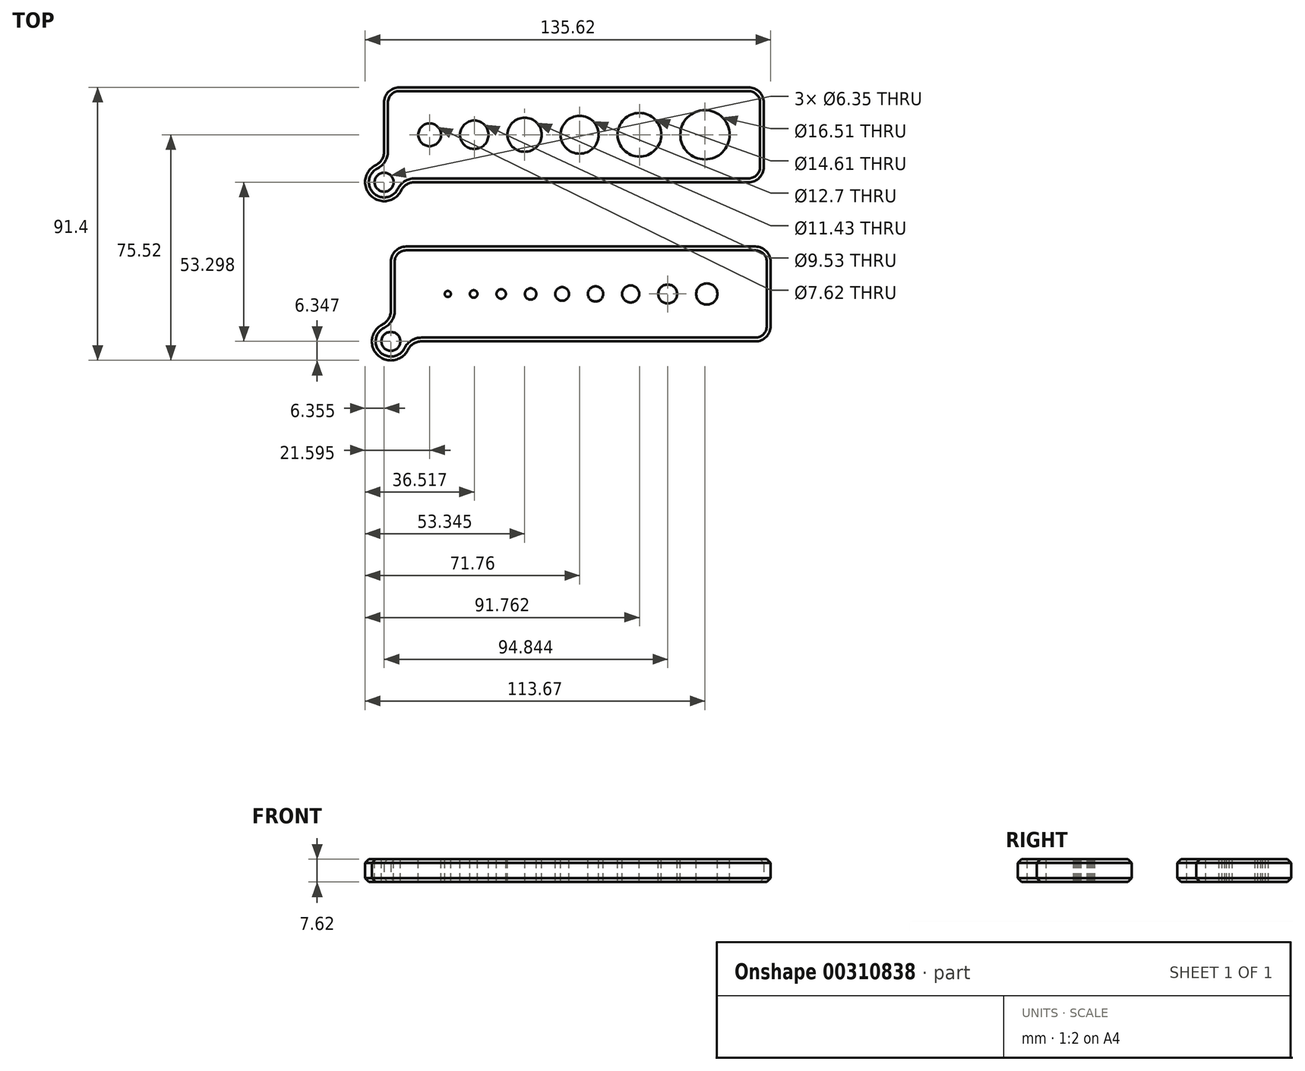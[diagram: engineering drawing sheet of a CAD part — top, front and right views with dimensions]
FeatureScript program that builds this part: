
annotation { "Feature Type Name" : "Feature", "Feature Type Description" : "" }
export const myFeature = defineFeature(function(context is Context, id is Id, definition is map)
    precondition{}
    {
        {
            var Q0;
            Q0=qCreatedBy(makeId("Top.planeOp"),FACE);
            var sketch = newSketch(context, id + "F0", { "sketchPlane" : qUnion([Q0])});
            skLineSegment(sketch, "E0.bottom", {"start": v(-62.35, 8.82) * mm, "end": v(64.65, 8.82) * mm});
            skLineSegment(sketch, "E0.top", {"start": v(-62.35, -22.93) * mm, "end": v(64.65, -22.93) * mm});
            skLineSegment(sketch, "E0.left", {"start": v(-62.35, 8.82) * mm, "end": v(-62.35, -22.93) * mm});
            skLineSegment(sketch, "E0.right", {"start": v(64.65, 8.82) * mm, "end": v(64.65, -22.93) * mm});
            skSolve(sketch);
        }
        {
            var Q0;
            Q0=makeQuery(id+"F0.imprint","IMPRINT",FACE,{"disambiguationData":[TD([[makeQuery(id+"F0.imprint","IMPRINT",EDGE,{"derivedFrom":sQuery(id+"F0.wireOp",EDGE,"E0.bottom")}),-1.0]])]});
            extrude(context, id + "F1", {"entities" : qUnion([Q0]), "depth" : 7.62 * mm});
        }
        {
            var Q0;
            Q0=makeQuery(id+"F1.opExtrude","CAP_FACE",FACE,{"disambiguationData":[OSD([sQuery(id+"F0.wireOp",EDGE,"E0.bottom"),sQuery(id+"F0.wireOp",EDGE,"E0.top"),sQuery(id+"F0.wireOp",EDGE,"E0.left"),sQuery(id+"F0.wireOp",EDGE,"E0.right")])],"isStart":false});
            var sketch = newSketch(context, id + "F2", { "sketchPlane" : qUnion([Q0])});
            skCircle(sketch, "E1", {"center": v(-43.3, -7.06) * mm, "radius": 1.02 * mm});
            skCircle(sketch, "E2", {"center": v(-34.67, -7.06) * mm, "radius": 1.27 * mm});
            skCircle(sketch, "E3", {"center": v(-25.46, -7.06) * mm, "radius": 1.59 * mm});
            skCircle(sketch, "E4", {"center": v(-15.62, -7.06) * mm, "radius": 1.9 * mm});
            skCircle(sketch, "E5", {"center": v(-5.08, -7.06) * mm, "radius": 2.29 * mm});
            skCircle(sketch, "E6", {"center": v(6.1, -7.06) * mm, "radius": 2.54 * mm});
            skCircle(sketch, "E7", {"center": v(17.85, -7.06) * mm, "radius": 2.86 * mm});
            skCircle(sketch, "E8", {"center": v(30.23, -7.06) * mm, "radius": 3.18 * mm});
            skCircle(sketch, "E9", {"center": v(43.31, -7.06) * mm, "radius": 3.56 * mm});
            skSolve(sketch);
        }
        {
            var Q0;
            Q0 = qSketchRegion(id + "F2", true);
            extrude(context, id + "F3", {"entities" : qUnion([Q0]), "operationType" : NewBodyOperationType.REMOVE, "oppositeDirection" : true, "depth" : 25.4 * mm});
        }
        {
            var Q0;
            Q0=qCreatedBy(makeId("Top.planeOp"),FACE);
            var sketch = newSketch(context, id + "F4", { "sketchPlane" : qUnion([Q0])});
            skLineSegment(sketch, "E10.bottom", {"start": v(-64.62, 62.12) * mm, "end": v(62.38, 62.12) * mm});
            skLineSegment(sketch, "E10.top", {"start": v(-64.62, 30.37) * mm, "end": v(62.38, 30.37) * mm});
            skLineSegment(sketch, "E10.left", {"start": v(-64.62, 62.12) * mm, "end": v(-64.62, 30.37) * mm});
            skLineSegment(sketch, "E10.right", {"start": v(62.38, 62.12) * mm, "end": v(62.38, 30.37) * mm});
            skSolve(sketch);
        }
        {
            var Q0;
            Q0=makeQuery(id+"F4.imprint","IMPRINT",FACE,{"disambiguationData":[TD([[makeQuery(id+"F4.imprint","IMPRINT",EDGE,{"derivedFrom":sQuery(id+"F4.wireOp",EDGE,"E10.bottom")}),-1.0]])]});
            extrude(context, id + "F5", {"entities" : qUnion([Q0]), "depth" : 7.62 * mm});
        }
        {
            var Q0;
            Q0=makeQuery(id+"F5.opExtrude","CAP_FACE",FACE,{"disambiguationData":[OSD([sQuery(id+"F4.wireOp",EDGE,"E10.bottom"),sQuery(id+"F4.wireOp",EDGE,"E10.top"),sQuery(id+"F4.wireOp",EDGE,"E10.left"),sQuery(id+"F4.wireOp",EDGE,"E10.right")])],"isStart":false});
            var sketch = newSketch(context, id + "F6", { "sketchPlane" : qUnion([Q0])});
            skCircle(sketch, "E11", {"center": v(-49.38, 46.24) * mm, "radius": 3.81 * mm});
            skPoint(sketch, "E11.centerSnap0", {"position": v(-64.62, 46.24) * mm});
            skCircle(sketch, "E12", {"center": v(-34.45, 46.24) * mm, "radius": 4.76 * mm});
            skCircle(sketch, "E13", {"center": v(-17.63, 46.24) * mm, "radius": 5.72 * mm});
            skCircle(sketch, "E14", {"center": v(0.79, 46.24) * mm, "radius": 6.35 * mm});
            skCircle(sketch, "E15", {"center": v(20.8, 46.24) * mm, "radius": 7.3 * mm});
            skCircle(sketch, "E16", {"center": v(42.7, 46.24) * mm, "radius": 8.26 * mm});
            skSolve(sketch);
        }
        {
            var Q0;
            Q0 = qSketchRegion(id + "F6", true);
            extrude(context, id + "F7", {"entities" : qUnion([Q0]), "operationType" : NewBodyOperationType.REMOVE, "oppositeDirection" : true, "depth" : 25.4 * mm});
        }
        {
            var Q0;
            Q0=makeQuery(id+"F5.opExtrude","CAP_FACE",FACE,{"disambiguationData":[OSD([sQuery(id+"F4.wireOp",EDGE,"E10.bottom"),sQuery(id+"F4.wireOp",EDGE,"E10.top"),sQuery(id+"F4.wireOp",EDGE,"E10.left"),sQuery(id+"F4.wireOp",EDGE,"E10.right")])],"isStart":false});
            var sketch = newSketch(context, id + "F8", { "sketchPlane" : qUnion([Q0])});
            skLineSegment(sketch, "E17.bottom", {"start": v(-64.62, 30.37) * mm, "end": v(-70.97, 30.37) * mm});
            skLineSegment(sketch, "E17.top", {"start": v(-64.62, 24.02) * mm, "end": v(-70.97, 24.02) * mm});
            skLineSegment(sketch, "E17.left", {"start": v(-64.62, 30.37) * mm, "end": v(-64.62, 24.02) * mm});
            skLineSegment(sketch, "E17.right", {"start": v(-70.97, 30.37) * mm, "end": v(-70.97, 24.02) * mm});
            skLineSegment(sketch, "E18.bottom", {"start": v(-70.97, 30.37) * mm, "end": v(-64.62, 30.37) * mm});
            skLineSegment(sketch, "E18.top", {"start": v(-70.97, 36.72) * mm, "end": v(-64.62, 36.72) * mm});
            skLineSegment(sketch, "E18.left", {"start": v(-70.97, 30.37) * mm, "end": v(-70.97, 36.72) * mm});
            skLineSegment(sketch, "E18.right", {"start": v(-64.62, 30.37) * mm, "end": v(-64.62, 36.72) * mm});
            skLineSegment(sketch, "E19.bottom", {"start": v(-64.62, 24.02) * mm, "end": v(-58.27, 24.02) * mm});
            skLineSegment(sketch, "E19.top", {"start": v(-64.62, 30.37) * mm, "end": v(-58.27, 30.37) * mm});
            skLineSegment(sketch, "E19.left", {"start": v(-64.62, 24.02) * mm, "end": v(-64.62, 30.37) * mm});
            skLineSegment(sketch, "E19.right", {"start": v(-58.27, 24.02) * mm, "end": v(-58.27, 30.37) * mm});
            skSolve(sketch);
        }
        {
            var Q0;
            Q0 = qSketchRegion(id + "F8", true);
            extrude(context, id + "F9", {"entities" : qUnion([Q0]), "oppositeDirection" : true, "depth" : 7.62 * mm});
        }
        {
            var Q0;
            Q0=makeQuery(id+"F9.opExtrude","SWEPT_BODY",BODY,{"disambiguationData":[OSD([sQuery(id+"F8.wireOp",EDGE,"E17.top"),sQuery(id+"F8.wireOp",EDGE,"E17.right"),sQuery(id+"F8.wireOp",EDGE,"E18.top"),sQuery(id+"F8.wireOp",EDGE,"E18.left"),sQuery(id+"F8.wireOp",EDGE,"E18.right"),sQuery(id+"F8.wireOp",EDGE,"E19.bottom"),sQuery(id+"F8.wireOp",EDGE,"E19.top"),sQuery(id+"F8.wireOp",EDGE,"E19.right")])]});
            var Q1;
            Q1=makeQuery(id+"F5.opExtrude","SWEPT_BODY",BODY,{"disambiguationData":[OSD([sQuery(id+"F4.wireOp",EDGE,"E10.bottom"),sQuery(id+"F4.wireOp",EDGE,"E10.top"),sQuery(id+"F4.wireOp",EDGE,"E10.left"),sQuery(id+"F4.wireOp",EDGE,"E10.right")])]});
            booleanBodies(context, id + "F10", {"operationType" : BooleanOperationType.UNION, "tools" : qUnion([Q0, Q1])});
        }
        {
            var Q0;
            Q0=makeQuery(id+"F9.opExtrude","SWEPT_EDGE",EDGE,{"disambiguationData":[OSD([sQuery(id+"F8.wireOp",EDGE,"E19.bottom"),sQuery(id+"F8.wireOp",EDGE,"E19.right")])]});
            var Q1;
            Q1=makeQuery(id+"F9.opExtrude","SWEPT_EDGE",EDGE,{"disambiguationData":[OSD([sQuery(id+"F8.wireOp",EDGE,"E17.top"),sQuery(id+"F8.wireOp",EDGE,"E17.right")])]});
            var Q2;
            Q2=makeQuery(id+"F9.opExtrude","SWEPT_EDGE",EDGE,{"disambiguationData":[OSD([sQuery(id+"F8.wireOp",EDGE,"E18.top"),sQuery(id+"F8.wireOp",EDGE,"E18.left")])]});
            fillet(context, id + "F11", {"entities" : qUnion([Q0, Q1, Q2]), "radius" : 6.35 * mm, "tangentPropagation" : true, "allowEdgeOverflow" : false});
        }
        {
            var Q0;
            Q0=makeQuery(id+"F1.opExtrude","CAP_FACE",FACE,{"disambiguationData":[OSD([sQuery(id+"F0.wireOp",EDGE,"E0.bottom"),sQuery(id+"F0.wireOp",EDGE,"E0.top"),sQuery(id+"F0.wireOp",EDGE,"E0.left"),sQuery(id+"F0.wireOp",EDGE,"E0.right")])],"isStart":false});
            var sketch = newSketch(context, id + "F12", { "sketchPlane" : qUnion([Q0])});
            skLineSegment(sketch, "E20.bottom", {"start": v(-62.35, -22.93) * mm, "end": v(-68.7, -22.93) * mm});
            skLineSegment(sketch, "E20.top", {"start": v(-62.35, -29.28) * mm, "end": v(-68.7, -29.28) * mm});
            skLineSegment(sketch, "E20.left", {"start": v(-62.35, -22.93) * mm, "end": v(-62.35, -29.28) * mm});
            skLineSegment(sketch, "E20.right", {"start": v(-68.7, -22.93) * mm, "end": v(-68.7, -29.28) * mm});
            skLineSegment(sketch, "E21.bottom", {"start": v(-62.35, -29.28) * mm, "end": v(-56, -29.28) * mm});
            skLineSegment(sketch, "E21.top", {"start": v(-62.35, -22.93) * mm, "end": v(-56, -22.93) * mm});
            skLineSegment(sketch, "E21.left", {"start": v(-62.35, -29.28) * mm, "end": v(-62.35, -22.93) * mm});
            skLineSegment(sketch, "E21.right", {"start": v(-56, -29.28) * mm, "end": v(-56, -22.93) * mm});
            skLineSegment(sketch, "E22.bottom", {"start": v(-68.7, -22.93) * mm, "end": v(-62.35, -22.93) * mm});
            skLineSegment(sketch, "E22.top", {"start": v(-68.7, -16.58) * mm, "end": v(-62.35, -16.58) * mm});
            skLineSegment(sketch, "E22.left", {"start": v(-68.7, -22.93) * mm, "end": v(-68.7, -16.58) * mm});
            skLineSegment(sketch, "E22.right", {"start": v(-62.35, -22.93) * mm, "end": v(-62.35, -16.58) * mm});
            skSolve(sketch);
        }
        {
            var Q0;
            Q0 = qSketchRegion(id + "F12", true);
            extrude(context, id + "F13", {"entities" : qUnion([Q0]), "operationType" : NewBodyOperationType.ADD, "oppositeDirection" : true, "depth" : 7.62 * mm});
        }
        {
            var Q0;
            Q0=makeQuery(id+"F13.opExtrude","SWEPT_EDGE",EDGE,{"disambiguationData":[OSD([sQuery(id+"F12.wireOp",EDGE,"E21.bottom"),sQuery(id+"F12.wireOp",EDGE,"E21.right")])]});
            var Q1;
            Q1=makeQuery(id+"F13.opExtrude","SWEPT_EDGE",EDGE,{"disambiguationData":[OSD([sQuery(id+"F12.wireOp",EDGE,"E20.top"),sQuery(id+"F12.wireOp",EDGE,"E20.right")])]});
            var Q2;
            Q2=makeQuery(id+"F13.opExtrude","SWEPT_EDGE",EDGE,{"disambiguationData":[OSD([sQuery(id+"F12.wireOp",EDGE,"E22.top"),sQuery(id+"F12.wireOp",EDGE,"E22.left")])]});
            fillet(context, id + "F14", {"entities" : qUnion([Q0, Q1, Q2]), "radius" : 6.35 * mm, "tangentPropagation" : true, "allowEdgeOverflow" : false});
        }
        {
            var Q0;
            Q0=makeQuery(id+"F13.boolean.opBoolean","MERGE",FACE,{"derivedFrom":[makeQuery(id+"F1.opExtrude","CAP_FACE",FACE,{"disambiguationData":[OSD([sQuery(id+"F0.wireOp",EDGE,"E0.bottom"),sQuery(id+"F0.wireOp",EDGE,"E0.top"),sQuery(id+"F0.wireOp",EDGE,"E0.left"),sQuery(id+"F0.wireOp",EDGE,"E0.right")])],"isStart":false}),makeQuery(id+"F13.opExtrude","CAP_FACE",FACE,{"disambiguationData":[OSD([sQuery(id+"F12.wireOp",EDGE,"E20.top"),sQuery(id+"F12.wireOp",EDGE,"E20.right"),sQuery(id+"F12.wireOp",EDGE,"E21.bottom"),sQuery(id+"F12.wireOp",EDGE,"E21.top"),sQuery(id+"F12.wireOp",EDGE,"E21.right"),sQuery(id+"F12.wireOp",EDGE,"E22.top"),sQuery(id+"F12.wireOp",EDGE,"E22.left"),sQuery(id+"F12.wireOp",EDGE,"E22.right")])],"isStart":true})]});
            var sketch = newSketch(context, id + "F15", { "sketchPlane" : qUnion([Q0])});
            skCircle(sketch, "E23", {"center": v(-62.35, -22.93) * mm, "radius": 3.18 * mm});
            skSolve(sketch);
        }
        {
            var Q0;
            Q0=makeQuery(id+"F10.opBoolean","MERGE",FACE,{"derivedFrom":[makeQuery(id+"F5.opExtrude","CAP_FACE",FACE,{"disambiguationData":[OSD([sQuery(id+"F4.wireOp",EDGE,"E10.bottom"),sQuery(id+"F4.wireOp",EDGE,"E10.top"),sQuery(id+"F4.wireOp",EDGE,"E10.left"),sQuery(id+"F4.wireOp",EDGE,"E10.right")])],"isStart":false}),makeQuery(id+"F9.opExtrude","CAP_FACE",FACE,{"disambiguationData":[OSD([sQuery(id+"F8.wireOp",EDGE,"E17.top"),sQuery(id+"F8.wireOp",EDGE,"E17.right"),sQuery(id+"F8.wireOp",EDGE,"E18.top"),sQuery(id+"F8.wireOp",EDGE,"E18.left"),sQuery(id+"F8.wireOp",EDGE,"E18.right"),sQuery(id+"F8.wireOp",EDGE,"E19.bottom"),sQuery(id+"F8.wireOp",EDGE,"E19.top"),sQuery(id+"F8.wireOp",EDGE,"E19.right")])],"isStart":true})]});
            var sketch = newSketch(context, id + "F16", { "sketchPlane" : qUnion([Q0])});
            skCircle(sketch, "E24", {"center": v(-64.62, 30.37) * mm, "radius": 3.18 * mm});
            skSolve(sketch);
        }
        {
            var Q0;
            Q0=makeQuery(id+"F16.imprint","IMPRINT",FACE,{"disambiguationData":[TD([[makeQuery(id+"F16.imprint","IMPRINT",EDGE,{"derivedFrom":sQuery(id+"F16.wireOp",EDGE,"E24")}),1.0]])]});
            extrude(context, id + "F17", {"entities" : qUnion([Q0]), "operationType" : NewBodyOperationType.REMOVE, "oppositeDirection" : true, "depth" : 25.4 * mm});
        }
        {
            var Q0;
            Q0=makeQuery(id+"F15.imprint","IMPRINT",FACE,{"disambiguationData":[TD([[makeQuery(id+"F15.imprint","IMPRINT",EDGE,{"derivedFrom":sQuery(id+"F15.wireOp",EDGE,"E23")}),1.0]])]});
            extrude(context, id + "F18", {"entities" : qUnion([Q0]), "operationType" : NewBodyOperationType.REMOVE, "oppositeDirection" : true, "depth" : 25.4 * mm});
        }
        {
            var Q0;
            Q0=makeQuery(id+"F14.opFillet","BLEND_EDGE",EDGE,{"blendedFrom":[makeQuery(id+"F13.opExtrude","SWEPT_EDGE",EDGE,{"disambiguationData":[OSD([sQuery(id+"F12.wireOp",EDGE,"E21.bottom"),sQuery(id+"F12.wireOp",EDGE,"E21.right")])]}),makeQuery(id+"F1.opExtrude","SWEPT_FACE",FACE,{"disambiguationData":[OSD([sQuery(id+"F0.wireOp",EDGE,"E0.top")])]})],"blendedInto":[makeQuery(id+"F1.opExtrude","SWEPT_FACE",FACE,{"disambiguationData":[OSD([sQuery(id+"F0.wireOp",EDGE,"E0.top")])]})]});
            var Q1;
            Q1=makeQuery(id+"F1.opExtrude","SWEPT_EDGE",EDGE,{"disambiguationData":[OSD([sQuery(id+"F0.wireOp",EDGE,"E0.top"),sQuery(id+"F0.wireOp",EDGE,"E0.right")])]});
            var Q2;
            Q2=makeQuery(id+"F1.opExtrude","SWEPT_EDGE",EDGE,{"disambiguationData":[OSD([sQuery(id+"F0.wireOp",EDGE,"E0.bottom"),sQuery(id+"F0.wireOp",EDGE,"E0.right")])]});
            var Q3;
            Q3=makeQuery(id+"F1.opExtrude","SWEPT_EDGE",EDGE,{"disambiguationData":[OSD([sQuery(id+"F0.wireOp",EDGE,"E0.bottom"),sQuery(id+"F0.wireOp",EDGE,"E0.left")])]});
            var Q4;
            Q4=makeQuery(id+"F14.opFillet","BLEND_EDGE",EDGE,{"blendedFrom":[makeQuery(id+"F13.opExtrude","SWEPT_EDGE",EDGE,{"disambiguationData":[OSD([sQuery(id+"F12.wireOp",EDGE,"E22.top"),sQuery(id+"F12.wireOp",EDGE,"E22.left")])]}),makeQuery(id+"F1.opExtrude","SWEPT_FACE",FACE,{"disambiguationData":[OSD([sQuery(id+"F0.wireOp",EDGE,"E0.left")])]})],"blendedInto":[makeQuery(id+"F1.opExtrude","SWEPT_FACE",FACE,{"disambiguationData":[OSD([sQuery(id+"F0.wireOp",EDGE,"E0.left")])]})]});
            var Q5;
            Q5=makeQuery(id+"F11.opFillet","BLEND_EDGE",EDGE,{"blendedFrom":[makeQuery(id+"F9.opExtrude","SWEPT_EDGE",EDGE,{"disambiguationData":[OSD([sQuery(id+"F8.wireOp",EDGE,"E18.top"),sQuery(id+"F8.wireOp",EDGE,"E18.left")])]}),makeQuery(id+"F5.opExtrude","SWEPT_FACE",FACE,{"disambiguationData":[OSD([sQuery(id+"F4.wireOp",EDGE,"E10.left")])]})],"blendedInto":[makeQuery(id+"F5.opExtrude","SWEPT_FACE",FACE,{"disambiguationData":[OSD([sQuery(id+"F4.wireOp",EDGE,"E10.left")])]})]});
            var Q6;
            Q6=makeQuery(id+"F5.opExtrude","SWEPT_EDGE",EDGE,{"disambiguationData":[OSD([sQuery(id+"F4.wireOp",EDGE,"E10.bottom"),sQuery(id+"F4.wireOp",EDGE,"E10.left")])]});
            var Q7;
            Q7=makeQuery(id+"F5.opExtrude","SWEPT_EDGE",EDGE,{"disambiguationData":[OSD([sQuery(id+"F4.wireOp",EDGE,"E10.bottom"),sQuery(id+"F4.wireOp",EDGE,"E10.right")])]});
            var Q8;
            Q8=makeQuery(id+"F11.opFillet","BLEND_EDGE",EDGE,{"blendedFrom":[makeQuery(id+"F9.opExtrude","SWEPT_EDGE",EDGE,{"disambiguationData":[OSD([sQuery(id+"F8.wireOp",EDGE,"E19.bottom"),sQuery(id+"F8.wireOp",EDGE,"E19.right")])]}),makeQuery(id+"F5.opExtrude","SWEPT_FACE",FACE,{"disambiguationData":[OSD([sQuery(id+"F4.wireOp",EDGE,"E10.top")])]})],"blendedInto":[makeQuery(id+"F5.opExtrude","SWEPT_FACE",FACE,{"disambiguationData":[OSD([sQuery(id+"F4.wireOp",EDGE,"E10.top")])]})]});
            var Q9;
            Q9=makeQuery(id+"F5.opExtrude","SWEPT_EDGE",EDGE,{"disambiguationData":[OSD([sQuery(id+"F4.wireOp",EDGE,"E10.top"),sQuery(id+"F4.wireOp",EDGE,"E10.right")])]});
            fillet(context, id + "F19", {"entities" : qUnion([Q0, Q1, Q2, Q3, Q4, Q5, Q6, Q7, Q8, Q9]), "radius" : 5.08 * mm, "tangentPropagation" : true, "allowEdgeOverflow" : false});
        }
        {
            var Q0;
            Q0=makeQuery(id+"F1.opExtrude","CAP_EDGE",EDGE,{"disambiguationData":[OSD([sQuery(id+"F0.wireOp",EDGE,"E0.top")])],"isStart":false});
            var Q1;
            Q1=makeQuery(id+"F5.opExtrude","CAP_EDGE",EDGE,{"disambiguationData":[OSD([sQuery(id+"F4.wireOp",EDGE,"E10.top")])],"isStart":false});
            var Q2;
            Q2=makeQuery(id+"F1.opExtrude","CAP_EDGE",EDGE,{"disambiguationData":[OSD([sQuery(id+"F0.wireOp",EDGE,"E0.top")])],"isStart":true});
            var Q3;
            Q3=makeQuery(id+"F5.opExtrude","CAP_EDGE",EDGE,{"disambiguationData":[OSD([sQuery(id+"F4.wireOp",EDGE,"E10.top")])],"isStart":true});
            chamfer(context, id + "F20", {"entities" : qUnion([Q0, Q1, Q2, Q3]), "width" : 1.27 * mm, "tangentPropagation" : true});
        }
    });
